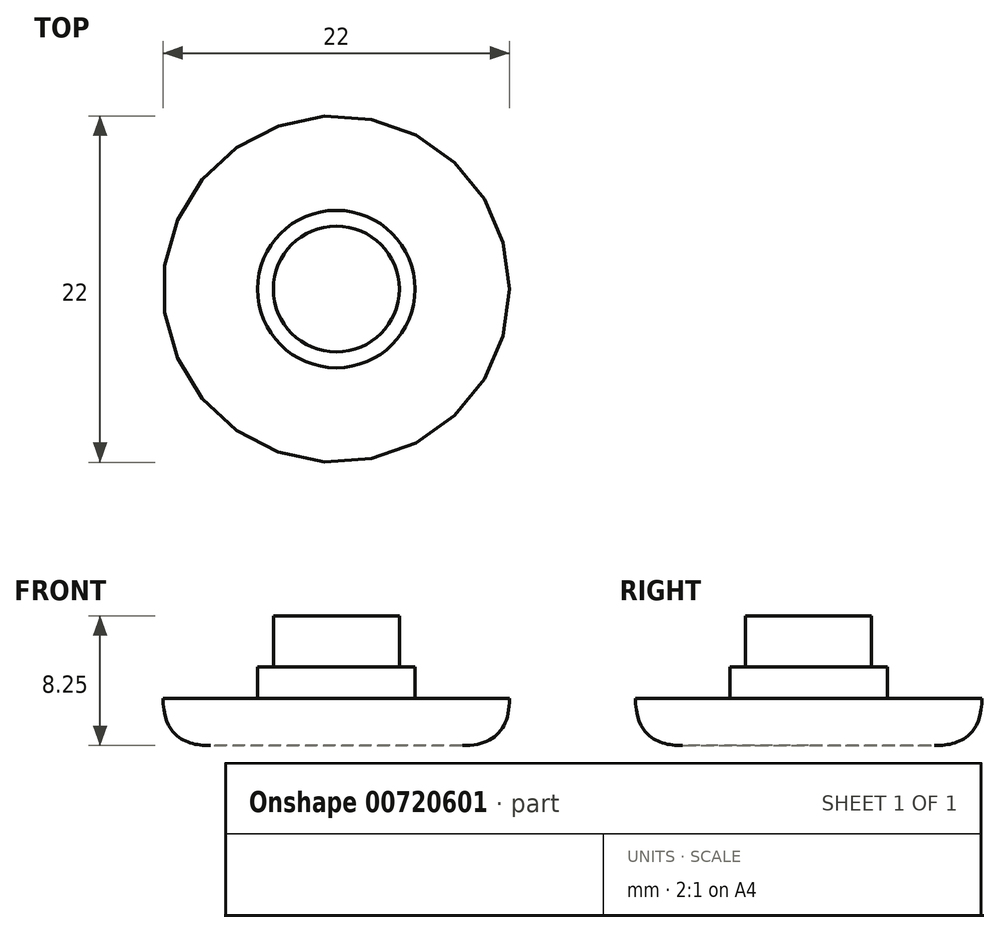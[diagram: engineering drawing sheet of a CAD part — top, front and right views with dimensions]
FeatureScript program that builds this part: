
annotation { "Feature Type Name" : "Feature", "Feature Type Description" : "" }
export const myFeature = defineFeature(function(context is Context, id is Id, definition is map)
    precondition{}
    {
        {
            var Q0;
            Q0=qCreatedBy(makeId("Top.planeOp"),FACE);
            var sketch = newSketch(context, id + "F0", { "sketchPlane" : qUnion([Q0])});
            skCircle(sketch, "E0", {"center": v(0, 0) * mm, "radius": 11 * mm});
            skSolve(sketch);
        }
        {
            var Q0;
            Q0=qCreatedBy(makeId("Top.planeOp"),FACE);
            var sketch = newSketch(context, id + "F1", { "sketchPlane" : qUnion([Q0])});
            skCircle(sketch, "E1", {"center": v(0, 0) * mm, "radius": 5 * mm});
            skSolve(sketch);
        }
        {
            var Q0;
            Q0=qCreatedBy(makeId("Top.planeOp"),FACE);
            var sketch = newSketch(context, id + "F2", { "sketchPlane" : qUnion([Q0])});
            skCircle(sketch, "E2", {"center": v(0, 0) * mm, "radius": 4 * mm});
            skSolve(sketch);
        }
        {
            var Q0;
            Q0=makeQuery(id+"F0.imprint","IMPRINT",FACE,{"disambiguationData":[TD([[makeQuery(id+"F0.imprint","IMPRINT",EDGE,{"derivedFrom":sQuery(id+"F0.wireOp",EDGE,"E0")}),1.0]])]});
            extrude(context, id + "F3", {"entities" : qUnion([Q0]), "depth" : 0 * mm, "offsetDistance" : 25 * mm, "hasSecondDirection" : true, "secondDirectionOppositeDirection" : true, "secondDirectionDepth" : 3 * mm});
        }
        {
            var Q0;
            Q0=qSketchRegion(id+"F1",true);
            extrude(context, id + "F4", {"entities" : qUnion([Q0]), "operationType" : NewBodyOperationType.ADD, "depth" : 2 * mm, "offsetDistance" : 25 * mm});
        }
        {
            var Q0;
            Q0=qSketchRegion(id+"F2",true);
            extrude(context, id + "F5", {"entities" : qUnion([Q0]), "operationType" : NewBodyOperationType.ADD, "depth" : 5.25 * mm, "offsetDistance" : 25 * mm});
        }
        {
            var Q0;
            Q0=makeQuery(id+"F3.opExtrude","CAP_EDGE",EDGE,{"disambiguationData":[OSD([sQuery(id+"F0.wireOp",EDGE,"E0")])],"isStart":true});
            fillet(context, id + "F6", {"entities" : qUnion([Q0]), "radius" : 3 * mm, "tangentPropagation" : true, "rho" : 0.5, "crossSection" : FilletCrossSection.CONIC, "allowEdgeOverflow" : false});
        }
    });
